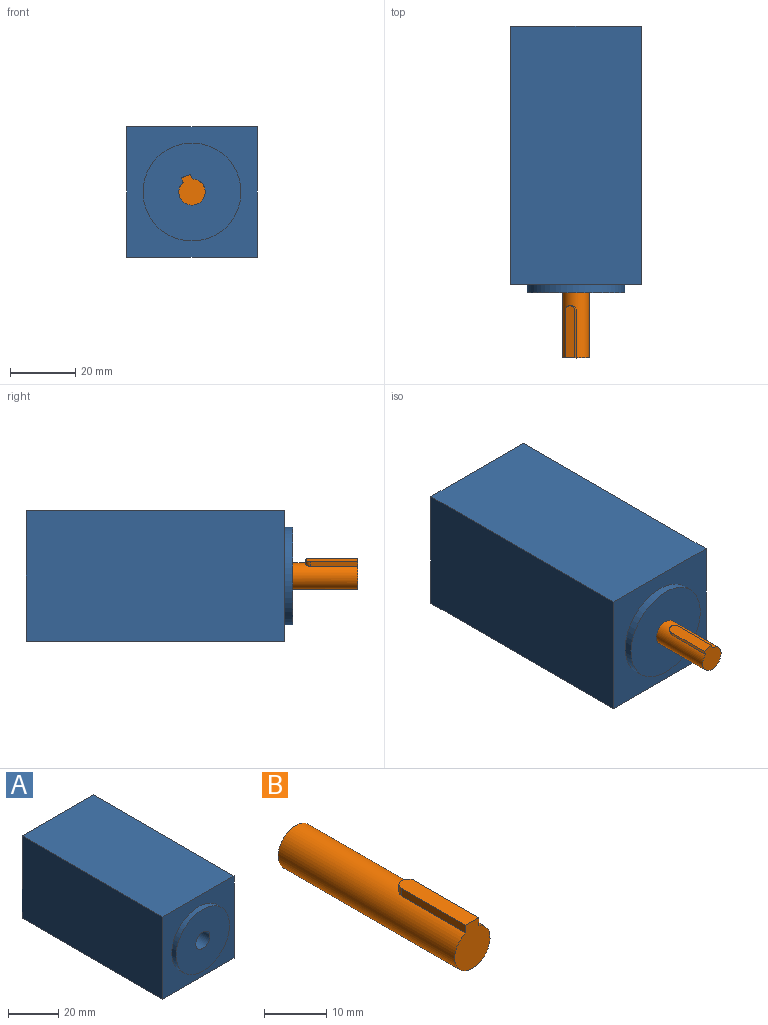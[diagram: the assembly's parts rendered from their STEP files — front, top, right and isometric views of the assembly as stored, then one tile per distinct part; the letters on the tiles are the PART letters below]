
ASSEMBLY  parts=2 mates=1
PART A: 10 faces, bbox 40x81.6x40 mm
  f0: plane 79.1x40mm, normal (0,0,1), area 3164mm2, adj f1,f3,f4,f5
  f1: plane 79.1x40mm, normal (-1,0,0), area 3164mm2, adj f0,f2,f4,f5
  f2: plane 79.1x40mm, normal (0,0,-1), area 3164mm2, adj f1,f3,f4,f5
  f3: plane 79.1x40mm, normal (1,0,0), area 3164mm2, adj f0,f2,f4,f5
  f4: plane 40x40mm, normal (0,-1,0), area 893.1mm2, adj f0,f1,f2,f3,f6
  f5: plane 40x40mm, normal (0,1,0), area 1600mm2, adj f0,f1,f2,f3
  f6: cylinder r=15mm len=30mm, axis (0,1,0), area 235.6mm2, adj f4,f7
  f7: plane 30x30mm, normal (0,-1,0), area 656.6mm2, adj f6,f8
  f8: cylinder r=4mm len=30mm, axis (0,-1,0), area 754mm2, adj f7,f9
  f9: plane 8x8mm, normal (0,-1,0), area 50.3mm2, adj f8
PART B: 7 faces, bbox 8x40x9.2 mm
  f0: cylinder r=4mm len=40mm, axis (0,1,0), area 957.1mm2, adj f1,f2,f3,f4,f6
  f1: plane 9.2x8mm, normal (0,-1,0), area 54.2mm2, adj f0,f3,f4,f5
  f2: plane 8x8mm, normal (0,1,0), area 50.3mm2, adj f0
  f3: plane 14.5x1.49mm, normal (-1,0,0), area 21.6mm2, adj f0,f1,f5,f6
  f4: plane 14.5x1.49mm, normal (1,0,0), area 21.6mm2, adj f0,f1,f5,f6
  f5: plane 16x3mm, normal (0,0,1), area 47mm2, adj f1,f3,f4,f6
  f6: cylinder r=1.5mm len=3mm, axis (0,0,-1), area 6.3mm2, adj f0,f3,f4,f5
PLACE A t=(-6.6,-3.11,-0.82)mm fixed
PLACE B rot(axis=(0,-1,0),20.8deg) t=(-6.6,-45.16,-0.82)mm
MATE revolute A.f8 <-> B.f0  axis (0,-1,0) through (-6.6,-45.16,-0.82)mm
